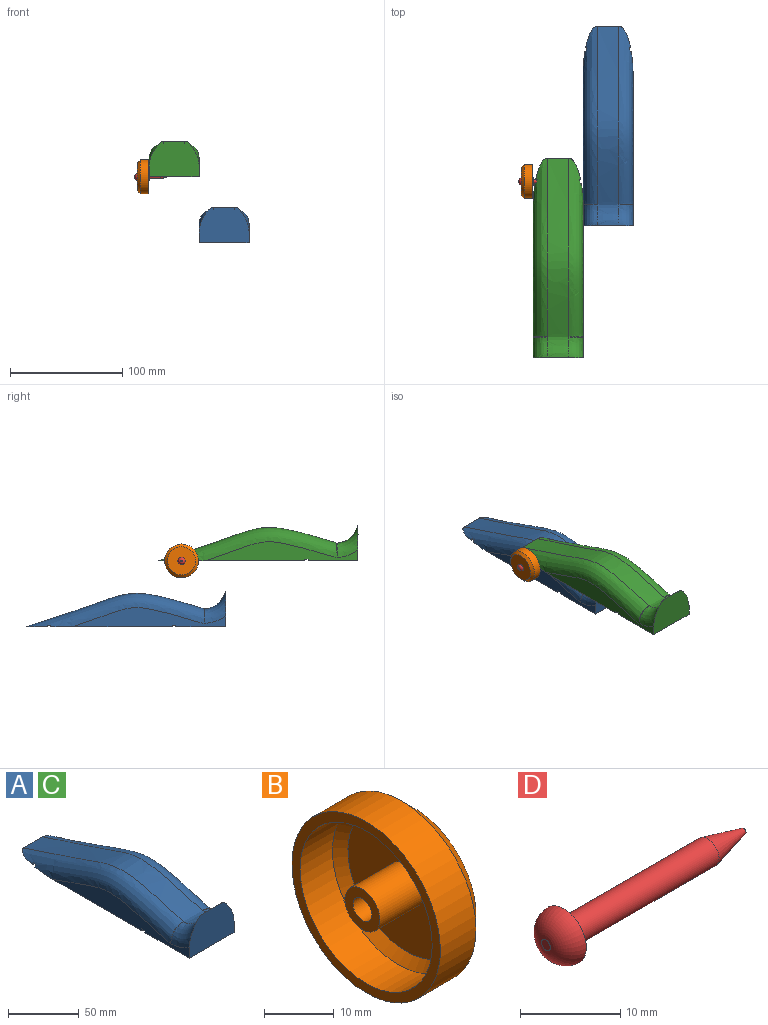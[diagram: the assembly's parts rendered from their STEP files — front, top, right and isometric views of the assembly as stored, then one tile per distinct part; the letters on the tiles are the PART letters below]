
ASSEMBLY  parts=4 mates=1
PART A: 19 faces, bbox 46.8x193.9x47.4 mm
  f0: plane 136.04x17.05mm, normal (1,0,0), area 1309.5mm2, adj f1,f4,f5,f9,f10,f11,f16,f18
  f1: plane 108.11x44.61mm, normal (0,0,-1), area 4778mm2, adj f0,f3,f8,f11,f15,f16
  f2: plane 40.11x19.06mm, normal (0,0,-1), area 643.4mm2, adj f6,f12,f15,f16
  f3: plane 136.04x17.05mm, normal (-1,0,0), area 1309.5mm2, adj f1,f4,f5,f9,f10,f11,f13,f15
  f4: plane 44.45x44.45mm, normal (0,0,-1), area 1975.8mm2, adj f0,f3,f5,f10
  f5: plane 46.75x34.05mm, normal (0,-1,0), area 1252.4mm2, adj f0,f3,f4,f12,f13,f18
  f6: plane 40.12x1.61mm, normal (0,-1,0), area 61.9mm2, adj f2,f7,f15,f16
  f7: plane 39.34x3.2mm, normal (0,0,-1), area 122.4mm2, adj f6,f8,f15,f16
  f8: plane 41.3x1.61mm, normal (0,1,0), area 64.1mm2, adj f1,f7,f15,f16
  f9: plane 44.45x3.18mm, normal (0,0,-1), area 141.1mm2, adj f0,f3,f10,f11
  f10: plane 44.45x1.59mm, normal (0,1,0), area 70.6mm2, adj f0,f3,f4,f9
  f11: plane 44.45x1.59mm, normal (0,-1,0), area 70.6mm2, adj f0,f1,f3,f9
  f12: extruded ~177.8x31.75mm, area 3642.7mm2, adj f2,f5,f13,f14,f15,f16,f17,f18
  f13: bspline ~32.78x29.44mm, area 452mm2, adj f3,f5,f12,f14
  f14: bspline ~12.74x12.7mm, area 3.3mm2, adj f12,f13,f15
  f15: bspline ~160.8x42.32mm, area 2968.3mm2, adj f1,f2,f3,f6,f7,f8,f12,f14
  f16: bspline ~160.8x42.32mm, area 2968.3mm2, adj f0,f1,f2,f6,f7,f8,f12,f17
  f17: bspline ~12.74x12.7mm, area 4.3mm2, adj f12,f16,f18
  f18: bspline ~32.78x29.44mm, area 452mm2, adj f0,f5,f12,f17
PART B: 10 faces, bbox 10.5x30.1x30.1 mm
  f0: cylinder r=13.4mm len=26.8mm, axis (1,0,0), area 551.8mm2, adj f1,f8
  f1: cone r=13.4mm half-angle=45deg, axis (-1,0,0), area 176.3mm2, adj f0,f2
  f2: plane 23.65x23.65mm, normal (-1,0,0), area 399.6mm2, adj f1,f3
  f3: cylinder r=3.56mm len=8.89mm, axis (1,0,0), area 198.6mm2, adj f2,f4
  f4: plane 7.11x7.11mm, normal (-1,0,0), area 28.3mm2, adj f3,f9
  f5: plane 25.02x25.02mm, normal (1,0,0), area 480.2mm2, adj f6,f9
  f6: cone r=15.05mm half-angle=45deg, axis (-1,0,0), area 311mm2, adj f5,f7
  f7: cylinder r=15.05mm len=30.1mm, axis (1,0,0), area 684.5mm2, adj f6,f8
  f8: plane 30.1x30.1mm, normal (-1,0,0), area 147.6mm2, adj f0,f7
  f9: cylinder r=1.91mm len=10.54mm, axis (1,0,0), area 126.2mm2, adj f4,f5
PART C: same geometry as A
PART D: 6 faces, bbox 27.9x6.4x6.4 mm
  f0: cylinder r=1.59mm len=20.32mm, axis (1,0,0), area 202.7mm2, adj f3,f5
  f1: plane 0.64x0.64mm, normal (1,0,0), area 0.3mm2, adj f5
  f2: plane 1.27x1.27mm, normal (-1,0,0), area 1.3mm2, adj f4
  f3: plane 6.35x6.35mm, normal (1,0,0), area 23.8mm2, adj f0,f4
  f4: torus R=0.64mm, axis (-1,0,0), area 56.5mm2, adj f2,f3
  f5: cone r=0.32mm half-angle=14deg, axis (-1,0,0), area 31.3mm2, adj f0,f1
PLACE A t=(43.57,65.55,-45.35)mm
PLACE B rot(axis=(0,0.02,-1),180deg) t=(-23.1,104.85,-2.52)mm
PLACE C t=(-0.88,-52.31,13.36)mm fixed
PLACE D t=(-7.86,104.85,-2.52)mm
MATE planar C.f0 <-> A.f3  axis (1,0,0) through (21.35,17.99,3.61)mm
